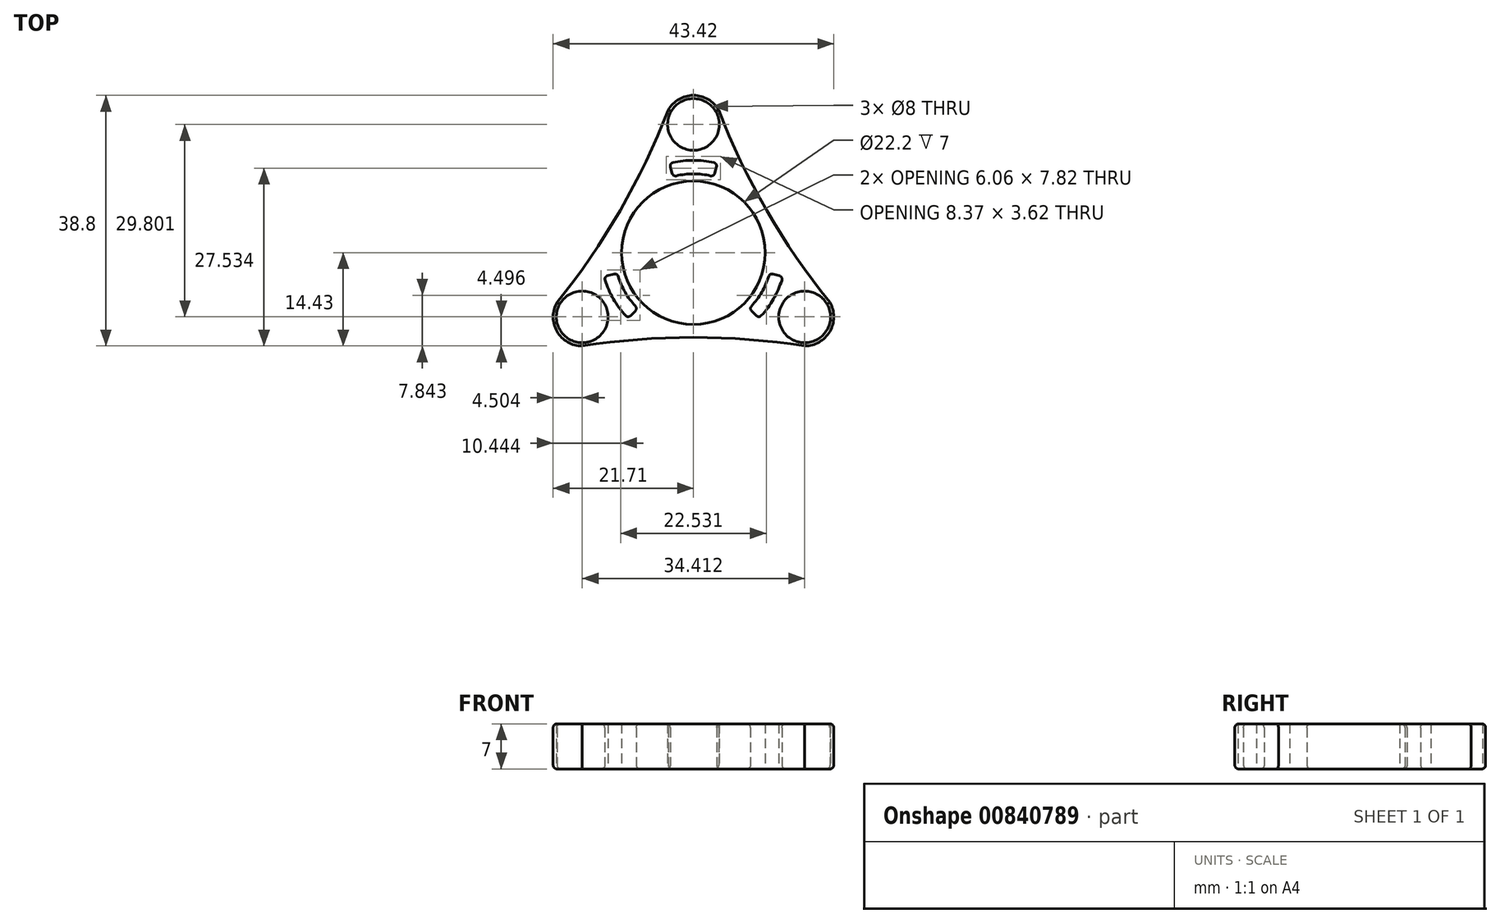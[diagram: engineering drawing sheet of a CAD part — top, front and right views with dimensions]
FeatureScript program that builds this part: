
annotation { "Feature Type Name" : "Feature", "Feature Type Description" : "" }
export const myFeature = defineFeature(function(context is Context, id is Id, definition is map)
    precondition{}
    {
        {
            var Q0;
            Q0=qCreatedBy(makeId("Top.planeOp"),FACE);
            var sketch = newSketch(context, id + "F0", { "sketchPlane" : qUnion([Q0])});
            skCircle(sketch, "E0", {"center": v(0, 0) * mm, "radius": 11.1 * mm});
            skPoint(sketch, "E1.start.orphan", {"position": v(0, 39.68) * mm});
            skPoint(sketch, "E2.orphan", {"position": v(25, -14.43) * mm});
            skPoint(sketch, "E3.orphan", {"position": v(-25, -14.43) * mm});
            skPoint(sketch, "E4.orphan", {"position": v(0, -14.43) * mm});
            skArc(sketch, "E5", {"start": v(-21.1, -7.68) * mm, "mid": v(-21.1, -12.18) * mm, "end": v(-17.2, -14.43) * mm});
            skArc(sketch, "E6", {"start": v(17.2, -14.43) * mm, "mid": v(21.1, -12.18) * mm, "end": v(21.1, -7.68) * mm});
            skArc(sketch, "E7", {"start": v(3.9, 22.12) * mm, "mid": v(0, 24.37) * mm, "end": v(-3.9, 22.12) * mm});
            skCircle(sketch, "E8", {"center": v(-17.2, -9.93) * mm, "radius": 4 * mm});
            skCircle(sketch, "E9", {"center": v(0, 19.87) * mm, "radius": 4 * mm});
            skCircle(sketch, "E10", {"center": v(17.2, -9.93) * mm, "radius": 4 * mm});
            skArc(sketch, "E11", {"start": v(-13.68, -4.22) * mm, "mid": v(-12.4, -7.16) * mm, "end": v(-10.5, -9.73) * mm});
            skArc(sketch, "E12", {"start": v(-11.65, -3.64) * mm, "mid": v(-10.57, -6.1) * mm, "end": v(-8.97, -8.27) * mm});
            skLineSegment(sketch, "E13", {"start": v(-12.28, -3.29) * mm, "end": v(-13.32, -3.57) * mm});
            skLineSegment(sketch, "E14", {"start": v(8.99, -8.99) * mm, "end": v(9.75, -9.75) * mm});
            skPoint(sketch, "E15.endSnap0", {"position": v(6.25, -3.6) * mm});
            skLineSegment(sketch, "E16", {"start": v(12.28, -3.29) * mm, "end": v(13.32, -3.57) * mm});
            skLineSegment(sketch, "E17.trimOffspring", {"start": v(-8.99, -8.99) * mm, "end": v(-9.75, -9.75) * mm});
            skLineSegment(sketch, "E18", {"start": v(-3.29, 12.28) * mm, "end": v(-3.57, 13.32) * mm});
            skLineSegment(sketch, "E19.trimOffspring", {"start": v(3.29, 12.28) * mm, "end": v(3.57, 13.32) * mm});
            skArc(sketch, "E20.trimOffspring", {"start": v(8.97, -8.27) * mm, "mid": v(10.57, -6.1) * mm, "end": v(11.65, -3.64) * mm});
            skArc(sketch, "E21.trimOffspring", {"start": v(10.5, -9.73) * mm, "mid": v(12.4, -7.16) * mm, "end": v(13.68, -4.22) * mm});
            skArc(sketch, "E22.trimOffspring", {"start": v(2.68, 11.9) * mm, "mid": v(0, 12.2) * mm, "end": v(-2.68, 11.9) * mm});
            skArc(sketch, "E23.trimOffspring", {"start": v(3.18, 13.95) * mm, "mid": v(0, 14.31) * mm, "end": v(-3.18, 13.95) * mm});
            skPoint(sketch, "E24.visualSharp", {"position": v(-3.16, 11.79) * mm});
            skArc(sketch, "E24.filletArc", {"start": v(-3.29, 12.28) * mm, "mid": v(-3.06, 11.97) * mm, "end": v(-2.68, 11.9) * mm});
            skPoint(sketch, "E25.visualSharp", {"position": v(3.16, 11.79) * mm});
            skArc(sketch, "E25.filletArc", {"start": v(2.68, 11.9) * mm, "mid": v(3.06, 11.97) * mm, "end": v(3.29, 12.28) * mm});
            skPoint(sketch, "E26.visualSharp", {"position": v(3.7, 13.83) * mm});
            skArc(sketch, "E26.filletArc", {"start": v(3.57, 13.32) * mm, "mid": v(3.51, 13.72) * mm, "end": v(3.18, 13.95) * mm});
            skPoint(sketch, "E27.visualSharp", {"position": v(-3.7, 13.83) * mm});
            skArc(sketch, "E27.filletArc", {"start": v(-3.18, 13.95) * mm, "mid": v(-3.51, 13.72) * mm, "end": v(-3.57, 13.32) * mm});
            skPoint(sketch, "E28.visualSharp", {"position": v(13.83, -3.7) * mm});
            skArc(sketch, "E28.filletArc", {"start": v(13.68, -4.22) * mm, "mid": v(13.64, -3.82) * mm, "end": v(13.32, -3.57) * mm});
            skPoint(sketch, "E29.visualSharp", {"position": v(11.79, -3.16) * mm});
            skArc(sketch, "E29.filletArc", {"start": v(12.28, -3.29) * mm, "mid": v(11.9, -3.34) * mm, "end": v(11.65, -3.64) * mm});
            skPoint(sketch, "E30.visualSharp", {"position": v(8.63, -8.63) * mm});
            skArc(sketch, "E30.filletArc", {"start": v(8.97, -8.27) * mm, "mid": v(8.84, -8.63) * mm, "end": v(8.99, -8.99) * mm});
            skPoint(sketch, "E31.visualSharp", {"position": v(10.12, -10.12) * mm});
            skArc(sketch, "E31.filletArc", {"start": v(9.75, -9.75) * mm, "mid": v(10.12, -9.9) * mm, "end": v(10.5, -9.73) * mm});
            skPoint(sketch, "E32.visualSharp", {"position": v(-13.83, -3.7) * mm});
            skArc(sketch, "E32.filletArc", {"start": v(-13.32, -3.57) * mm, "mid": v(-13.64, -3.82) * mm, "end": v(-13.68, -4.22) * mm});
            skPoint(sketch, "E33.visualSharp", {"position": v(-11.79, -3.16) * mm});
            skArc(sketch, "E33.filletArc", {"start": v(-11.65, -3.64) * mm, "mid": v(-11.9, -3.34) * mm, "end": v(-12.28, -3.29) * mm});
            skPoint(sketch, "E34.visualSharp", {"position": v(-8.63, -8.63) * mm});
            skArc(sketch, "E34.filletArc", {"start": v(-8.99, -8.99) * mm, "mid": v(-8.84, -8.63) * mm, "end": v(-8.97, -8.27) * mm});
            skPoint(sketch, "E35.visualSharp", {"position": v(-10.12, -10.12) * mm});
            skArc(sketch, "E35.filletArc", {"start": v(-10.5, -9.73) * mm, "mid": v(-10.12, -9.9) * mm, "end": v(-9.75, -9.75) * mm});
            skArc(sketch, "E36", {"start": v(-21.1, -7.68) * mm, "mid": v(-11.34, 6.55) * mm, "end": v(-3.9, 22.12) * mm});
            skArc(sketch, "E37", {"start": v(3.9, 22.12) * mm, "mid": v(11.34, 6.55) * mm, "end": v(21.1, -7.68) * mm});
            skArc(sketch, "E38", {"start": v(17.2, -14.43) * mm, "mid": v(0, -13.1) * mm, "end": v(-17.2, -14.43) * mm});
            skSolve(sketch);
        }
        {
            var Q0;
            Q0=makeQuery(id+"F0.imprint","IMPRINT",FACE,{"disambiguationData":[TD([[makeQuery(id+"F0.imprint","IMPRINT",EDGE,{"derivedFrom":sQuery(id+"F0.wireOp",EDGE,"E0")}),-1.0]])]});
            extrude(context, id + "F1", {"entities" : qUnion([Q0]), "depth" : 7 * mm, "offsetDistance" : 25 * mm});
        }
        {
            var Q0;
            Q0=makeQuery(id+"F1.opExtrude","CAP_EDGE",EDGE,{"disambiguationData":[OSD([sQuery(id+"F0.wireOp",EDGE,"E36")])],"isStart":false});
            var Q1;
            Q1=makeQuery(id+"F1.opExtrude","CAP_EDGE",EDGE,{"disambiguationData":[OSD([sQuery(id+"F0.wireOp",EDGE,"E37")])],"isStart":false});
            var Q2;
            Q2=makeQuery(id+"F1.opExtrude","CAP_EDGE",EDGE,{"disambiguationData":[OSD([sQuery(id+"F0.wireOp",EDGE,"E7")])],"isStart":false});
            var Q3;
            Q3=makeQuery(id+"F1.opExtrude","CAP_EDGE",EDGE,{"disambiguationData":[OSD([sQuery(id+"F0.wireOp",EDGE,"E5")])],"isStart":false});
            var Q4;
            Q4=makeQuery(id+"F1.opExtrude","CAP_EDGE",EDGE,{"disambiguationData":[OSD([sQuery(id+"F0.wireOp",EDGE,"E38")])],"isStart":false});
            var Q5;
            Q5=makeQuery(id+"F1.opExtrude","CAP_EDGE",EDGE,{"disambiguationData":[OSD([sQuery(id+"F0.wireOp",EDGE,"E6")])],"isStart":false});
            var Q6;
            Q6=makeQuery(id+"F1.opExtrude","CAP_EDGE",EDGE,{"disambiguationData":[OSD([sQuery(id+"F0.wireOp",EDGE,"E20.trimOffspring")])],"isStart":false});
            var Q7;
            Q7=makeQuery(id+"F1.opExtrude","CAP_EDGE",EDGE,{"disambiguationData":[OSD([sQuery(id+"F0.wireOp",EDGE,"E12")])],"isStart":false});
            var Q8;
            Q8=makeQuery(id+"F1.opExtrude","CAP_EDGE",EDGE,{"disambiguationData":[OSD([sQuery(id+"F0.wireOp",EDGE,"E23.trimOffspring")])],"isStart":false});
            var Q9;
            Q9=makeQuery(id+"F1.opExtrude","CAP_EDGE",EDGE,{"disambiguationData":[OSD([sQuery(id+"F0.wireOp",EDGE,"E23.trimOffspring")])],"isStart":true});
            var Q10;
            Q10=makeQuery(id+"F1.opExtrude","CAP_EDGE",EDGE,{"disambiguationData":[OSD([sQuery(id+"F0.wireOp",EDGE,"E21.trimOffspring")])],"isStart":true});
            var Q11;
            Q11=makeQuery(id+"F1.opExtrude","CAP_EDGE",EDGE,{"disambiguationData":[OSD([sQuery(id+"F0.wireOp",EDGE,"E11")])],"isStart":true});
            var Q12;
            Q12=makeQuery(id+"F1.opExtrude","CAP_EDGE",EDGE,{"disambiguationData":[OSD([sQuery(id+"F0.wireOp",EDGE,"E36")])],"isStart":true});
            var Q13;
            Q13=makeQuery(id+"F1.opExtrude","CAP_EDGE",EDGE,{"disambiguationData":[OSD([sQuery(id+"F0.wireOp",EDGE,"E5")])],"isStart":true});
            var Q14;
            Q14=makeQuery(id+"F1.opExtrude","CAP_EDGE",EDGE,{"disambiguationData":[OSD([sQuery(id+"F0.wireOp",EDGE,"E38")])],"isStart":true});
            var Q15;
            Q15=makeQuery(id+"F1.opExtrude","CAP_EDGE",EDGE,{"disambiguationData":[OSD([sQuery(id+"F0.wireOp",EDGE,"E6")])],"isStart":true});
            var Q16;
            Q16=makeQuery(id+"F1.opExtrude","CAP_EDGE",EDGE,{"disambiguationData":[OSD([sQuery(id+"F0.wireOp",EDGE,"E37")])],"isStart":true});
            var Q17;
            Q17=makeQuery(id+"F1.opExtrude","CAP_EDGE",EDGE,{"disambiguationData":[OSD([sQuery(id+"F0.wireOp",EDGE,"E7")])],"isStart":true});
            fillet(context, id + "F2", {"entities" : qUnion([Q0, Q1, Q2, Q3, Q4, Q5, Q6, Q7, Q8, Q9, Q10, Q11, Q12, Q13, Q14, Q15, Q16, Q17]), "radius" : .6 * mm, "tangentPropagation" : true, "allowEdgeOverflow" : false});
        }
    });
